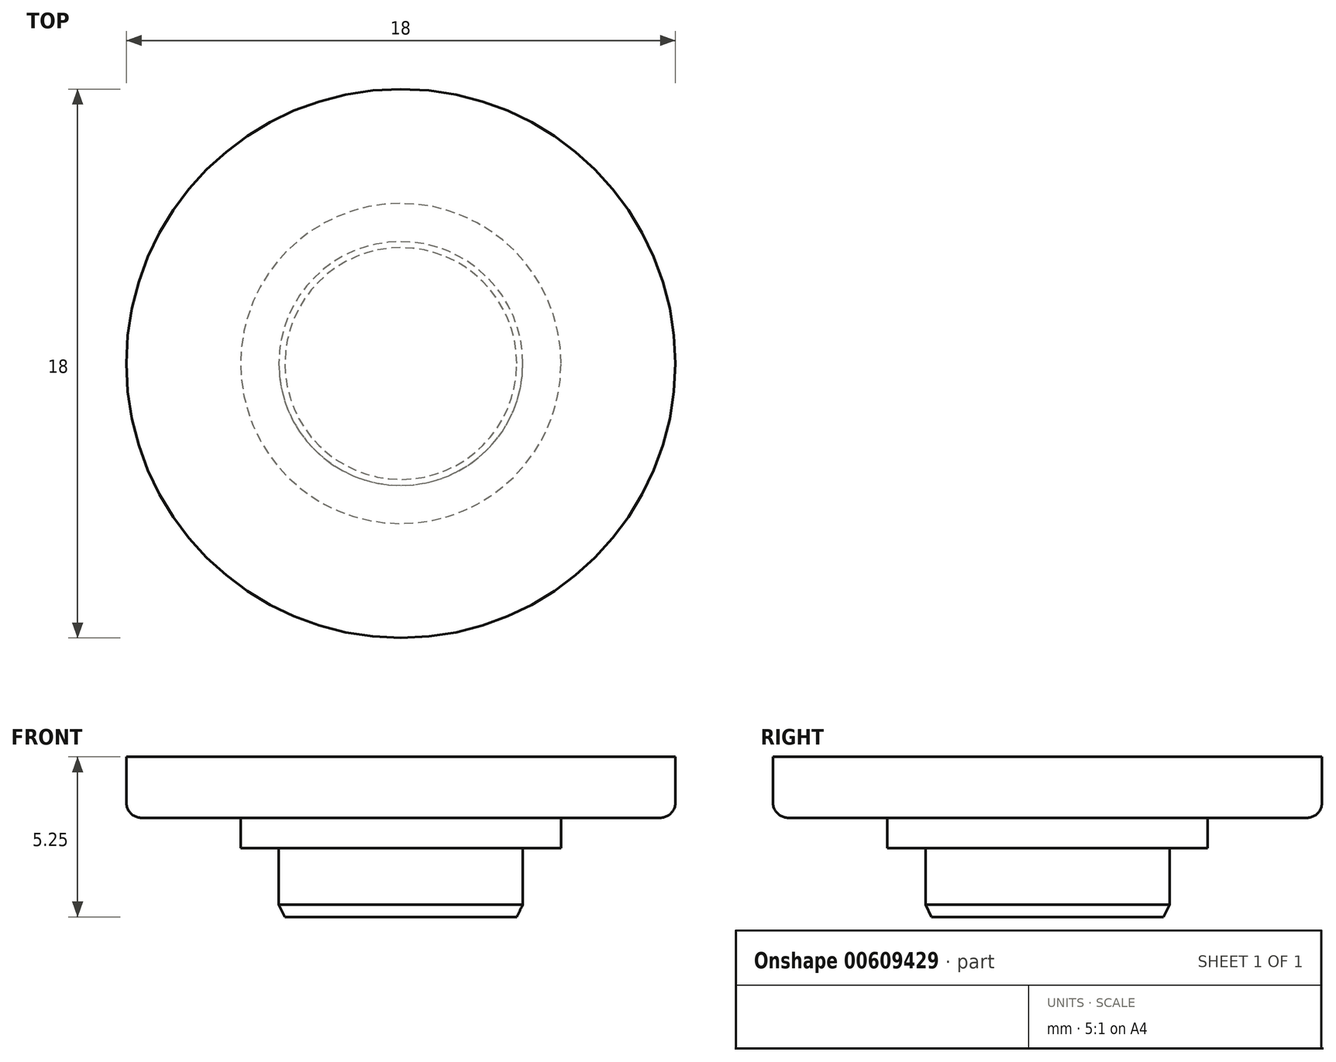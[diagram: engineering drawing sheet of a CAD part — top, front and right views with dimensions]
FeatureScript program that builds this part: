
annotation { "Feature Type Name" : "Feature", "Feature Type Description" : "" }
export const myFeature = defineFeature(function(context is Context, id is Id, definition is map)
    precondition{}
    {
        {
            var Q0;
            Q0=qCreatedBy(makeId("Front.planeOp"),FACE);
            var sketch = newSketch(context, id + "F0", { "sketchPlane" : qUnion([Q0])});
            skLineSegment(sketch, "E0", {"start": v(0, 0) * mm, "end": v(0, 5.25) * mm});
            skLineSegment(sketch, "E1", {"start": v(0, 5.25) * mm, "end": v(-9, 5.25) * mm});
            skLineSegment(sketch, "E2", {"start": v(-9, 5.25) * mm, "end": v(-9, 3.25) * mm});
            skLineSegment(sketch, "E3", {"start": v(-9, 3.25) * mm, "end": v(-5.25, 3.25) * mm});
            skLineSegment(sketch, "E4", {"start": v(-5.25, 3.25) * mm, "end": v(-5.25, 2.25) * mm});
            skLineSegment(sketch, "E5", {"start": v(-5.25, 2.25) * mm, "end": v(-4, 2.25) * mm});
            skLineSegment(sketch, "E6", {"start": v(-4, 2.25) * mm, "end": v(-4, 0) * mm});
            skLineSegment(sketch, "E7", {"start": v(-4, 0) * mm, "end": v(0, 0) * mm});
            skSolve(sketch);
        }
        {
            var Q0;
            Q0=makeQuery(id+"F0.imprint","IMPRINT",FACE,{"disambiguationData":[TD([[makeQuery(id+"F0.imprint","IMPRINT",EDGE,{"derivedFrom":sQuery(id+"F0.wireOp",EDGE,"E0")}),1.0]])]});
            var Q1;
            Q1=sQuery(id+"F0.wireOp",EDGE,"E0");
            revolve(context, id + "F1", {"entities" : qUnion([Q0]), "axis" : qUnion([Q1]), "revolveType" : RevolveType.FULL});
        }
        {
            var Q0;
            Q0=makeQuery(id+"F1.opRevolve","SWEPT_EDGE",EDGE,{"disambiguationData":[OSD([sQuery(id+"F0.wireOp",EDGE,"E2"),sQuery(id+"F0.wireOp",EDGE,"E3")])]});
            fillet(context, id + "F2", {"entities" : qUnion([Q0]), "radius" : .5 * mm, "tangentPropagation" : true, "allowEdgeOverflow" : false});
        }
        {
            var Q0;
            Q0=makeQuery(id+"F1.opRevolve","SWEPT_EDGE",EDGE,{"disambiguationData":[OSD([sQuery(id+"F0.wireOp",EDGE,"E6"),sQuery(id+"F0.wireOp",EDGE,"E7")])]});
            chamfer(context, id + "F3", {"entities" : qUnion([Q0]), "chamferType" : ChamferType.TWO_OFFSETS, "width1" : .2 * mm, "oppositeDirection" : false, "width2" : .4 * mm, "tangentPropagation" : true});
        }
    });
